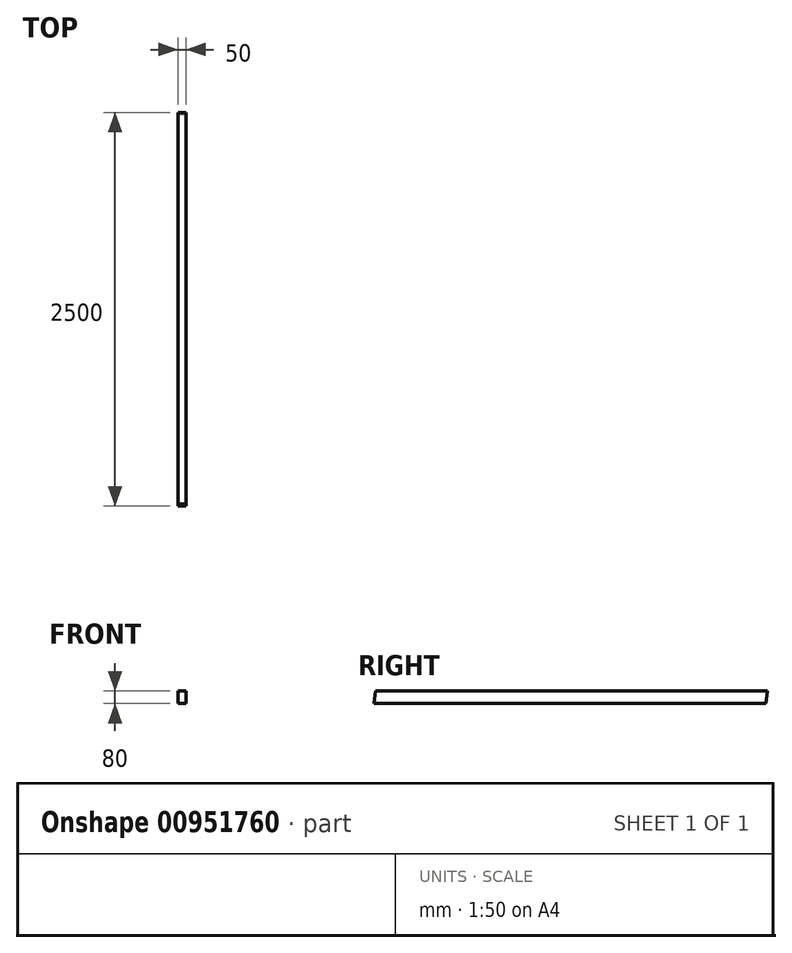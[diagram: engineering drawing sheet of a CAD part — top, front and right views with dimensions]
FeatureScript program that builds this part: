
annotation { "Feature Type Name" : "Feature", "Feature Type Description" : "" }
export const myFeature = defineFeature(function(context is Context, id is Id, definition is map)
    precondition{}
    {
        {
            var Q0;
            Q0=qCreatedBy(makeId("Front.planeOp"),FACE);
            var sketch = newSketch(context, id + "F0", { "sketchPlane" : qUnion([Q0])});
            skLineSegment(sketch, "E0.bottom", {"start": v(25, -40) * mm, "end": v(-25, -40) * mm});
            skLineSegment(sketch, "E0.top", {"start": v(25, 40) * mm, "end": v(-25, 40) * mm});
            skLineSegment(sketch, "E0.left", {"start": v(25, -40) * mm, "end": v(25, 40) * mm});
            skLineSegment(sketch, "E0.right", {"start": v(-25, -40) * mm, "end": v(-25, 40) * mm});
            skPoint(sketch, "E0.middle", {"position": v(0, 0) * mm});
            skSolve(sketch);
        }
        {
            var Q0;
            Q0 = qSketchRegion(id + "F0", true);
            extrude(context, id + "F1", {"entities" : qUnion([Q0]), "depth" : 2500 * mm, "offsetDistance" : 25 * mm});
        }
        {
            var Q0;
            Q0=makeQuery(id+"F1.opExtrude","SWEPT_FACE",FACE,{"disambiguationData":[OSD([sQuery(id+"F0.wireOp",EDGE,"E0.left")])]});
            var sketch = newSketch(context, id + "F2", { "sketchPlane" : qUnion([Q0])});
            skLineSegment(sketch, "E1", {"start": v(0, -40) * mm, "end": v(0, 40) * mm});
            skLineSegment(sketch, "E2", {"start": v(0, 40) * mm, "end": v(-11.24, -40) * mm});
            skLineSegment(sketch, "E3", {"start": v(-11.24, -40) * mm, "end": v(0, -40) * mm});
            skLineSegment(sketch, "E4", {"start": v(-2500, 40) * mm, "end": v(-2500, -40) * mm});
            skLineSegment(sketch, "E5", {"start": v(-2500, -40) * mm, "end": v(-2488.76, 40) * mm});
            skLineSegment(sketch, "E6", {"start": v(-2488.76, 40) * mm, "end": v(-2500, 40) * mm});
            skSolve(sketch);
        }
        {
            var Q0;
            Q0 = qSketchRegion(id + "F2", true);
            extrude(context, id + "F3", {"entities" : qUnion([Q0]), "operationType" : NewBodyOperationType.REMOVE, "oppositeDirection" : true, "depth" : 87.88 * mm, "offsetDistance" : 25 * mm});
        }
    });
